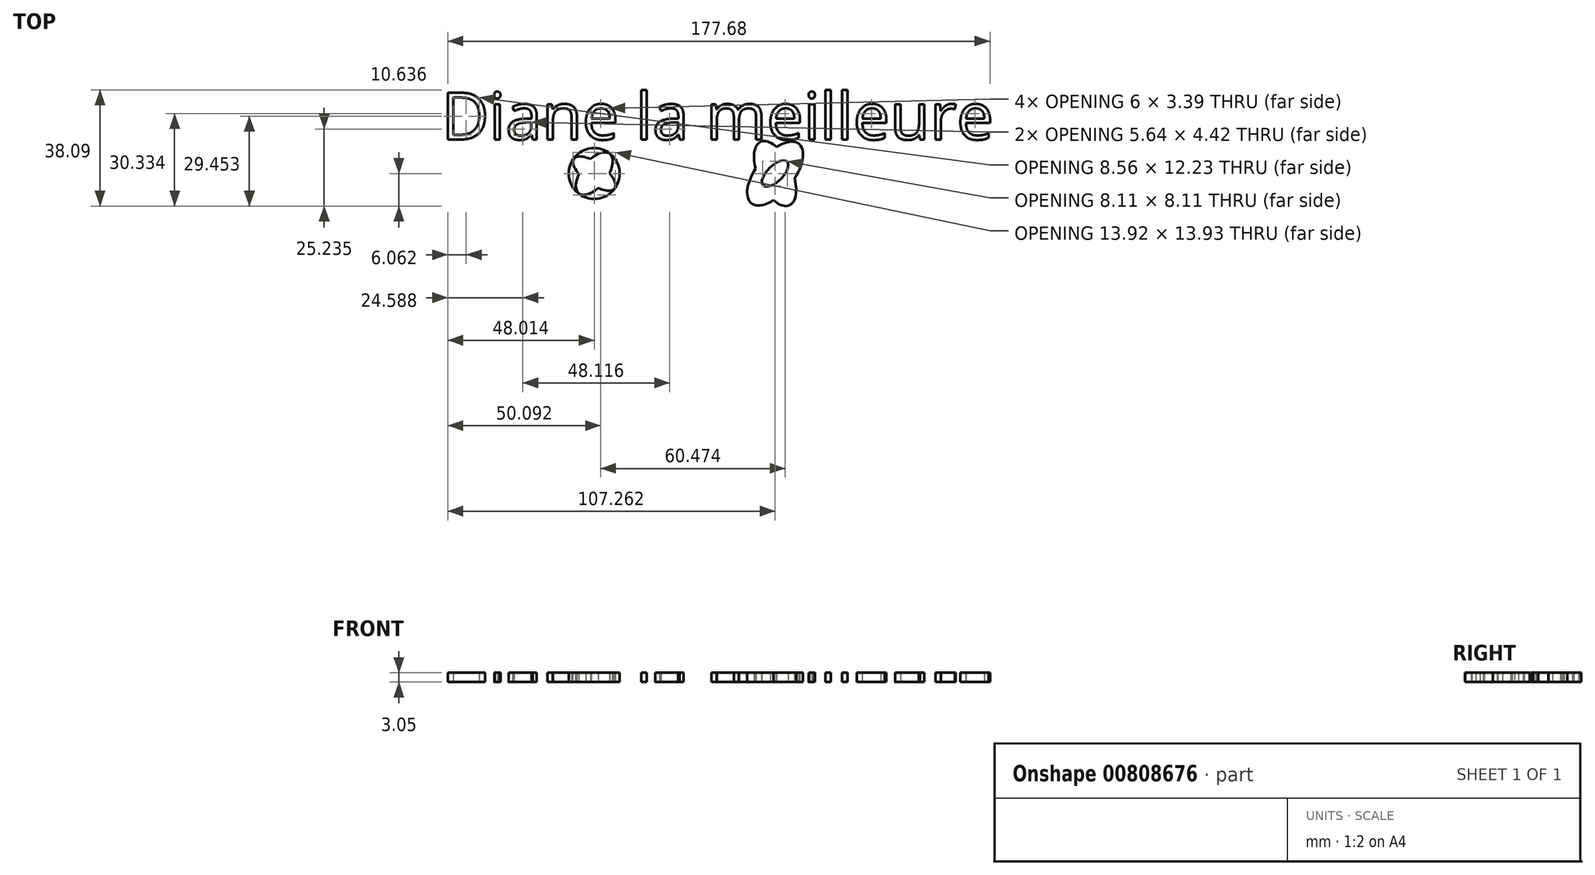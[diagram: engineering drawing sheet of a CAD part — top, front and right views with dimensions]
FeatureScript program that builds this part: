
annotation { "Feature Type Name" : "Feature", "Feature Type Description" : "" }
export const myFeature = defineFeature(function(context is Context, id is Id, definition is map)
    precondition{}
    {
        {
            var Q0;
            Q0=qCreatedBy(makeId("Top.planeOp"),FACE);
            var sketch = newSketch(context, id + "F0", { "sketchPlane" : qUnion([Q0])});
            skText(sketch, "E0", { "text": "Diane la meilleure\n\n", "fontName": "OpenSans-Regular.ttf"});
            skCircle(sketch, "E1", {"center": v(-38.2, 6.98) * mm, "radius": 8.35 * mm});
            skEllipse(sketch, "E2", {"center": v(-38.2, 6.98) * mm, "majorRadius": 8.25 * mm, "minorRadius": 3.5 * mm, "majorAxis": v(0.8, -0.6)});
            skEllipse(sketch, "E3", {"center": v(-38.2, 6.98) * mm, "majorRadius": 8.21 * mm, "minorRadius": 4.2 * mm, "majorAxis": v(0.61, 0.8)});
            skEllipse(sketch, "E4", {"center": v(21.05, 6.98) * mm, "majorRadius": 5.5 * mm, "minorRadius": 2.6 * mm, "majorAxis": v(-0.7, -0.7)});
            skEllipse(sketch, "E5", {"center": v(21.05, 6.98) * mm, "majorRadius": 11.4 * mm, "minorRadius": 5.54 * mm, "majorAxis": v(-0.41, 0.91)});
            skEllipse(sketch, "E6", {"center": v(21.05, 6.98) * mm, "majorRadius": 12.47 * mm, "minorRadius": 6.15 * mm, "majorAxis": v(0.62, 0.78)});
            const initialGuessF0  = {"E0": [-0.08831, 0.01814, 1, 0, 0.01544]};
            skSetInitialGuess(sketch, initialGuessF0);
            skSolve(sketch);
        }
        {
            var Q0;
            Q0 = qSketchRegion(id + "F0", true);
            extrude(context, id + "F1", {"entities" : qUnion([Q0]), "depth" : 3.05 * mm, "offsetDistance" : 25.4 * mm});
        }
    });
